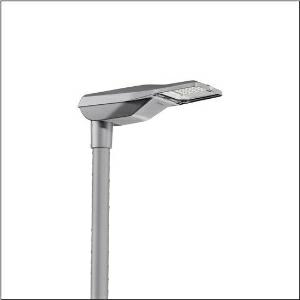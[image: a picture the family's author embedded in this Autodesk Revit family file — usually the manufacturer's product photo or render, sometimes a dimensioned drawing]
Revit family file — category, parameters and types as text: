
# Revit family: streetlight_sl_21_iq_micro___st0_8a_5xe1c41d08db_9d18
name_source: partatom
category: Lighting Fixtures
units: mm (PartAtom-declared; Revit-internal decimal feet)

## family parameters
Cut with Voids When Loaded = No
Host = Face
Light Source = No
Part Type = Normal
Room Calculation Point = No
Round Connector Dimension = Use Diameter
Shared = No

## types (1)
- --- (1 x LED, 5010 lm, 36.4 W, 4000K)
    Apparent Load = 36 VA
    CIE Flux Codes = 38 75 97 100 100
    Color Rendering = 70
    Color Temperature = 4000K
    Default Elevation = 1800 mm
    Description = Streetlight SL 21 iQ micro, mast luminaire, primary light control with lens, of PMMA, primary optical cover: cover, of toughened safety glass, transparent, light distribution: ST0.8a, light emission: direct distribution, primary light characteristic: asymmetric, installation type: post-top, side-entry, LED, High Power LED, rated luminous flux: 5.010lm, luminous efficacy: 138lm/W, light colour: 740, colour temperature: 4000K, control gear: iQ-Comfort, control: Auto-Match, Temp-Guard, Lumen-Switch, Night-Set, Smart-Wire, Light-Fading, Desk-Remote (wireless, voltage-free reading and setting of iQ features in the workshop via application-optimized NFC function/RFID function), optimised constant luminous flux control (CLO 2.0), pre-setting: linear dimming characteristic, mains connection: 220..240V, AC, 50/60Hz, start of lifetime: 36W, end of service life: 38W, reduction: 16W, luminaire housing, of diecast aluminium, powder-coated, Siteco® metallic grey (DB 702S), corrosivity category C5 mid according to DIN EN ISO 12944, please order mast flange separately, inclination adjustable: 0°, 5°, 10°, 15°, sealing non-destructively replaceable, multi-level sealing system, length: 528mm, width: 235mm, height: 110mm, mast flange for spigot size: 42mm (side-entry): 5XC10008XM4, 60/48mm (side-entry/post-top): 5XC10108XM2, 76/60mm (side-entry/post-top): 5XC10108XM1, protection rating (complete): IP66, insulation class (complete): insulation class II (safety insulation), certification: CE, ENEC, ENEC+, VDE, impact resistance: IK10, permissible operating ambient temperature for outdoor applications: -40..+50°C, standard-compliant lighting for roads and squares, packaging unit: 1 piece

Light Distribution: ST0.8a
    Height = 110 mm
    Lamp = 1 x LED
    Lamp Light Flux = 5010 lm
    Lamp Power = 36.4 W
    Lamp count = 1
    Length = 528 mm
    Luminous efficacy = 138 lm/W
    Manufacturer = Siteco
    ModVariant = No
    Model = 5XE1C41D08DB
    Number of Poles = 1
    OnlyDefault = Yes
    Power Factor = 1
    Product Name = Streetlight SL 21 iQ micro | ST0.8a
    Product group = mast luminaire | pylon top
    ProductGroupID = 6100
    Protection Class = Protection class II
    Protection Degree = IP 66
    RLX_Detail_Level = 1
    RLX_Emergency_Light_Flux = 0 lm
    RLX_Emergency_Type = 0
    RLX_Emergency_Type_DB = No
    RlxData = <blob elided: 99173 chars, md5=9032b64a>
    Socket = socket
    Standby Power = 0 W
    System Light Flux = 5010 lm
    System Power = 36 W
    Type Comments = factory setting: luminous flux: 100 % | dim-lin: 254 | 715 mA
    Type Image = l_1006881.jpg
    URL = http://relux.com
    VarID = @adj_175983
    Voltage = 0 V
    Weight = 0.00 kg
    Width = 235 mm

## geometry (parser evidence)
native form markers: Blend x4, Sweep x11
no freeform markers — native parametric forms only
